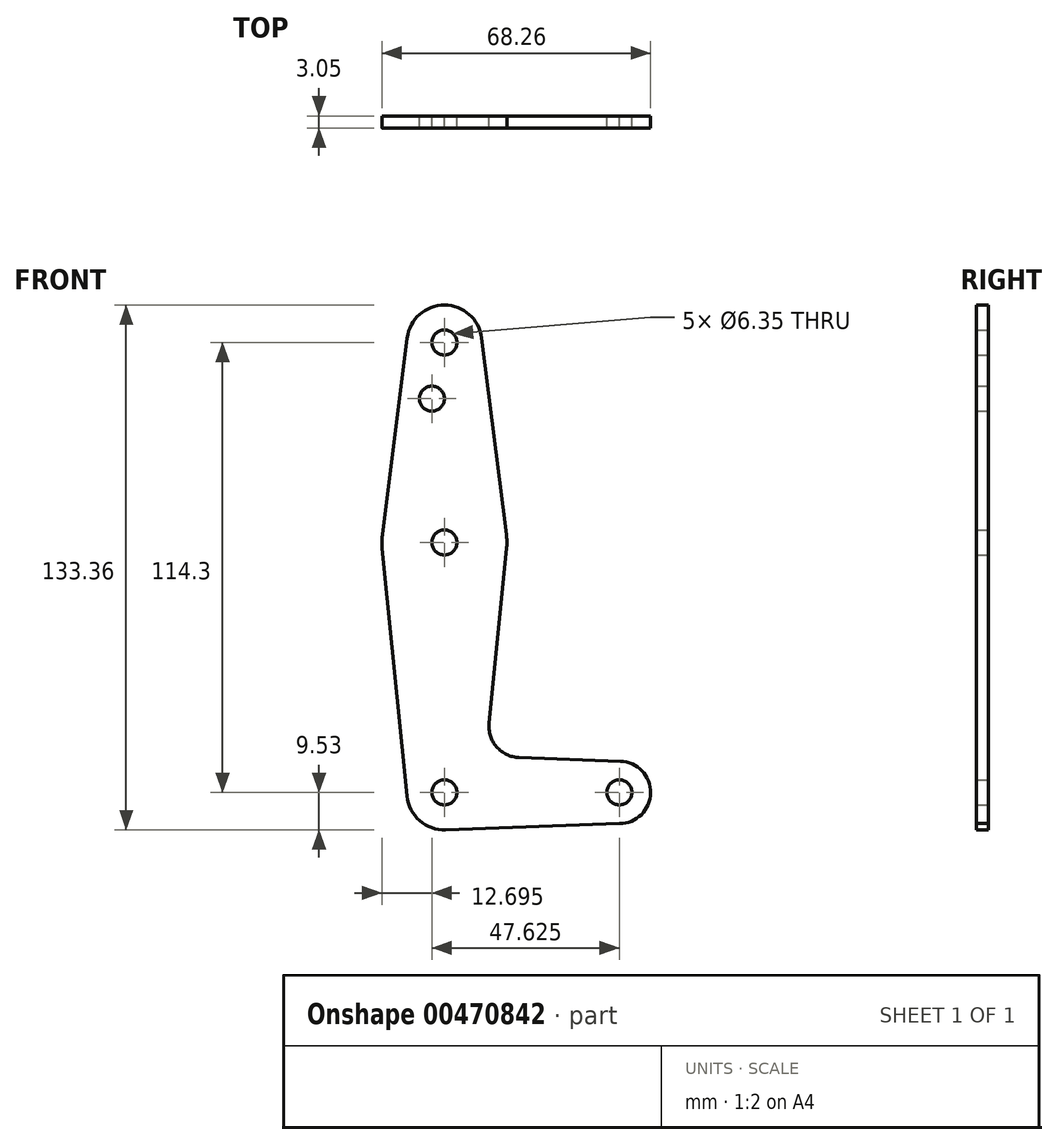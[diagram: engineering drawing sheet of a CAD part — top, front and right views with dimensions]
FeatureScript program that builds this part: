
annotation { "Feature Type Name" : "Feature", "Feature Type Description" : "" }
export const myFeature = defineFeature(function(context is Context, id is Id, definition is map)
    precondition{}
    {
        {
            var Q0;
            Q0=qCreatedBy(makeId("Front.planeOp"),FACE);
            var sketch = newSketch(context, id + "F0", { "sketchPlane" : qUnion([Q0])});
            skLineSegment(sketch, "E0", {"start": v(0, 0) * mm, "end": v(0, 114.3) * mm, "construction": true});
            skLineSegment(sketch, "E1", {"start": v(0, 0) * mm, "end": v(44.45, 0) * mm, "construction": true});
            skCircle(sketch, "E2", {"center": v(0, 114.3) * mm, "radius": 9.52 * mm});
            skCircle(sketch, "E3", {"center": v(0, 63.5) * mm, "radius": 15.88 * mm});
            skCircle(sketch, "E4", {"center": v(0, 0) * mm, "radius": 9.53 * mm});
            skCircle(sketch, "E5", {"center": v(44.45, 0) * mm, "radius": 7.94 * mm});
            skLineSegment(sketch, "E6", {"start": v(-15.75, 65.48) * mm, "end": v(-9.45, 115.5) * mm});
            skLineSegment(sketch, "E7", {"start": v(9.45, 115.5) * mm, "end": v(15.75, 65.48) * mm});
            skLineSegment(sketch, "E8", {"start": v(15.8, 61.91) * mm, "end": v(11.34, 17.6) * mm});
            skLineSegment(sketch, "E9", {"start": v(-9.48, -0.95) * mm, "end": v(-15.8, 61.91) * mm});
            skLineSegment(sketch, "E10", {"start": v(18.97, 8.85) * mm, "end": v(44.73, 7.93) * mm});
            skLineSegment(sketch, "E11", {"start": v(44.45, -7.94) * mm, "end": v(0, -9.53) * mm});
            skCircle(sketch, "E12", {"center": v(0, 114.3) * mm, "radius": 3.18 * mm});
            skCircle(sketch, "E13", {"center": v(0, 63.5) * mm, "radius": 3.18 * mm});
            skCircle(sketch, "E14", {"center": v(0, 0) * mm, "radius": 3.18 * mm});
            skCircle(sketch, "E15", {"center": v(44.45, 0) * mm, "radius": 3.18 * mm});
            skCircle(sketch, "E16", {"center": v(-3.18, 100.03) * mm, "radius": 3.18 * mm});
            skArc(sketch, "E17.filletArc", {"start": v(11.34, 17.6) * mm, "mid": v(13.26, 11.57) * mm, "end": v(18.97, 8.85) * mm});
            skSolve(sketch);
        }
        {
            var Q0;
            Q0 = qSketchRegion(id + "F0", true);
            extrude(context, id + "F1", {"entities" : qUnion([Q0]), "depth" : 3.05 * mm});
        }
    });
